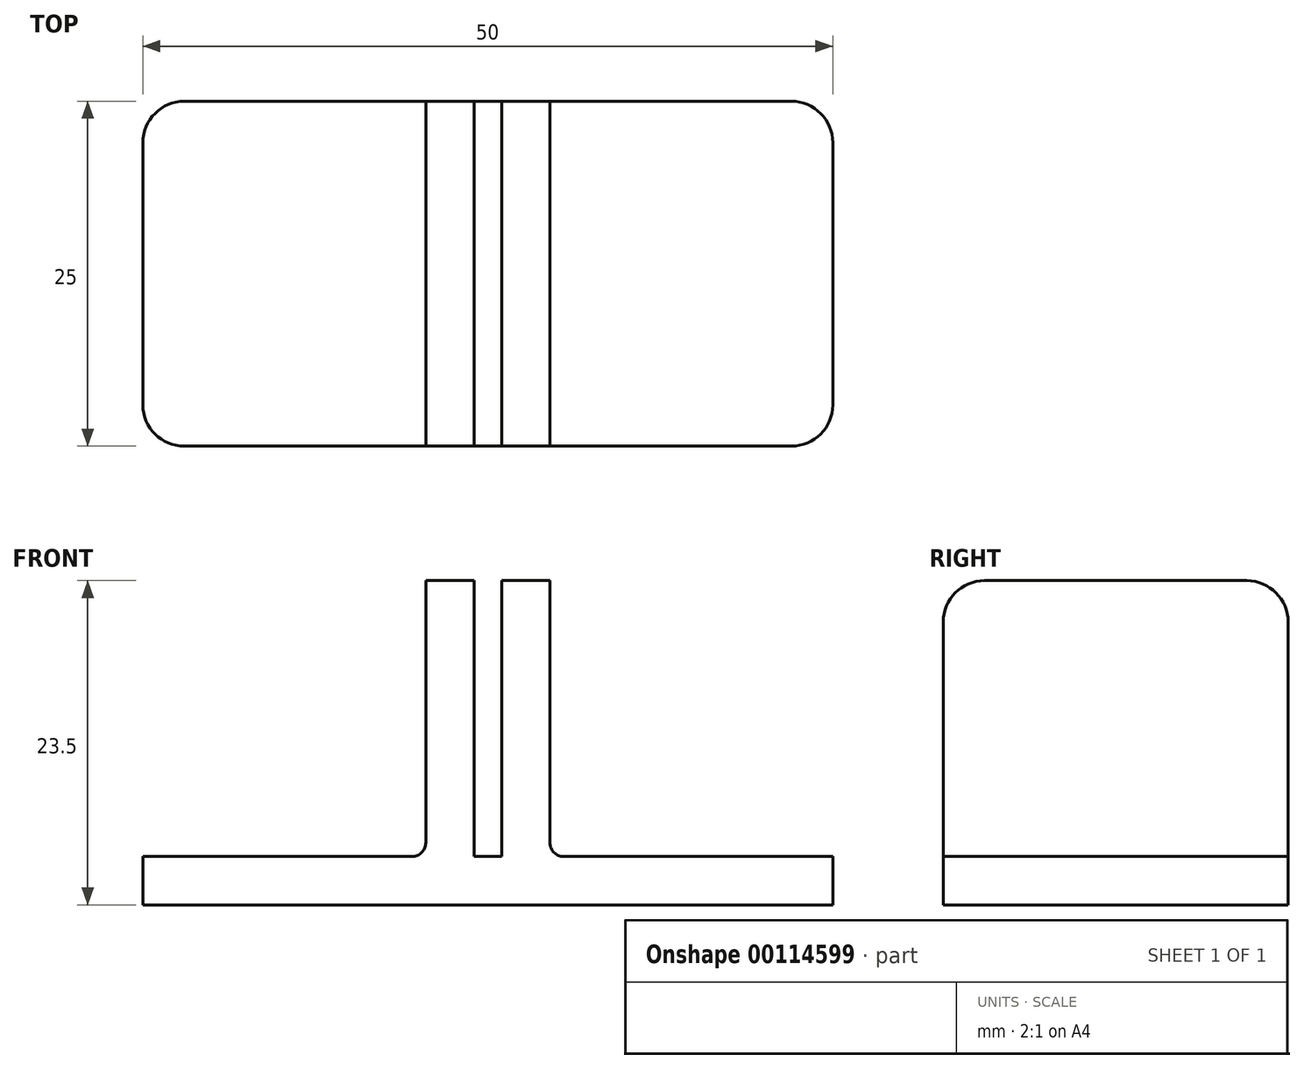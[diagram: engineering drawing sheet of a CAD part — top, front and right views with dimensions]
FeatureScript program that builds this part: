
annotation { "Feature Type Name" : "Feature", "Feature Type Description" : "" }
export const myFeature = defineFeature(function(context is Context, id is Id, definition is map)
    precondition{}
    {
        {
            var Q0;
            Q0=qCreatedBy(makeId("Front.planeOp"),FACE);
            var sketch = newSketch(context, id + "F0", { "sketchPlane" : qUnion([Q0])});
            skLineSegment(sketch, "E0", {"start": v(-25, 0) * mm, "end": v(25, 0) * mm});
            skLineSegment(sketch, "E1", {"start": v(25, 0) * mm, "end": v(25, 3.5) * mm});
            skLineSegment(sketch, "E2", {"start": v(25, 3.5) * mm, "end": v(4.5, 3.5) * mm});
            skLineSegment(sketch, "E3", {"start": v(4.5, 3.5) * mm, "end": v(4.5, 23.5) * mm});
            skLineSegment(sketch, "E4", {"start": v(4.5, 23.5) * mm, "end": v(1, 23.5) * mm});
            skLineSegment(sketch, "E5", {"start": v(1, 23.5) * mm, "end": v(1, 3.5) * mm});
            skLineSegment(sketch, "E6", {"start": v(1, 3.5) * mm, "end": v(-1, 3.5) * mm});
            skLineSegment(sketch, "E7", {"start": v(-1, 3.5) * mm, "end": v(-1, 23.5) * mm});
            skLineSegment(sketch, "E8", {"start": v(-1, 23.5) * mm, "end": v(-4.5, 23.5) * mm});
            skLineSegment(sketch, "E9", {"start": v(-4.5, 23.5) * mm, "end": v(-4.5, 3.5) * mm});
            skLineSegment(sketch, "E10", {"start": v(-4.5, 3.5) * mm, "end": v(-25, 3.5) * mm});
            skLineSegment(sketch, "E11", {"start": v(-25, 3.5) * mm, "end": v(-25, 0) * mm});
            skSolve(sketch);
        }
        {
            var Q0;
            Q0 = qSketchRegion(id + "F0", true);
            extrude(context, id + "F1", {"entities" : qUnion([Q0]), "depth" : 25 * mm});
        }
        {
            var Q0;
            Q0=makeQuery(id+"F1.opExtrude","CAP_EDGE",EDGE,{"disambiguationData":[OSD([sQuery(id+"F0.wireOp",EDGE,"E11")])],"isStart":false});
            var Q1;
            Q1=makeQuery(id+"F1.opExtrude","CAP_EDGE",EDGE,{"disambiguationData":[OSD([sQuery(id+"F0.wireOp",EDGE,"E11")])],"isStart":true});
            var Q2;
            Q2=makeQuery(id+"F1.opExtrude","CAP_EDGE",EDGE,{"disambiguationData":[OSD([sQuery(id+"F0.wireOp",EDGE,"E8")])],"isStart":true});
            var Q3;
            Q3=makeQuery(id+"F1.opExtrude","CAP_EDGE",EDGE,{"disambiguationData":[OSD([sQuery(id+"F0.wireOp",EDGE,"E8")])],"isStart":false});
            var Q4;
            Q4=makeQuery(id+"F1.opExtrude","CAP_EDGE",EDGE,{"disambiguationData":[OSD([sQuery(id+"F0.wireOp",EDGE,"E4")])],"isStart":false});
            var Q5;
            Q5=makeQuery(id+"F1.opExtrude","CAP_EDGE",EDGE,{"disambiguationData":[OSD([sQuery(id+"F0.wireOp",EDGE,"E4")])],"isStart":true});
            var Q6;
            Q6=makeQuery(id+"F1.opExtrude","CAP_EDGE",EDGE,{"disambiguationData":[OSD([sQuery(id+"F0.wireOp",EDGE,"E1")])],"isStart":false});
            var Q7;
            Q7=makeQuery(id+"F1.opExtrude","CAP_EDGE",EDGE,{"disambiguationData":[OSD([sQuery(id+"F0.wireOp",EDGE,"E1")])],"isStart":true});
            fillet(context, id + "F2", {"entities" : qUnion([Q0, Q1, Q2, Q3, Q4, Q5, Q6, Q7]), "radius" : 3 * mm, "tangentPropagation" : true, "allowEdgeOverflow" : false});
        }
        {
            var Q0;
            Q0=makeQuery(id+"F1.opExtrude","SWEPT_EDGE",EDGE,{"disambiguationData":[OSD([sQuery(id+"F0.wireOp",EDGE,"E9"),sQuery(id+"F0.wireOp",EDGE,"E10")])]});
            var Q1;
            Q1=makeQuery(id+"F1.opExtrude","SWEPT_EDGE",EDGE,{"disambiguationData":[OSD([sQuery(id+"F0.wireOp",EDGE,"E2"),sQuery(id+"F0.wireOp",EDGE,"E3")])]});
            fillet(context, id + "F3", {"entities" : qUnion([Q0, Q1]), "radius" : 1 * mm, "tangentPropagation" : true, "allowEdgeOverflow" : false});
        }
    });
